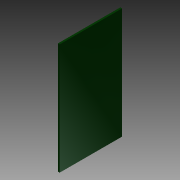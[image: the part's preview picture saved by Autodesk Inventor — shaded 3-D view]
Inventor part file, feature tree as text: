
AUTODESK INVENTOR PART (.ipt)
format: ipt  version: 2015 (Build 190159000, 159)  size: 87,040 bytes
history: native  units: in
note: dims shown in document units (in); Inventor stores cm internally (conversion verified against a paired STEP export)
features: extrude x1, sketch x1
ambient origin geometry x8: Origin, YZ Plane, XZ Plane, XY Plane, X Axis, Y Axis, Z Axis, Center Point
bodies: Solid1 (feature_tree)
feature tree (2):
  extrude  "Extrusion1"  Depth=2.25in
  sketch  "Sketch1"  dims[d0=4.0in d2=2.25in d3=0.0646in d4=0.0in]
